# Revit family: PM-套管伸缩节
name_source: partatom
category: 管道附件
revit_build: Autodesk Revit 2016 (Build: 20150220_1215(x64)
units: mm (PartAtom-declared; Revit-internal decimal feet)

## family parameters
共享 = 否
加载时剪切的空心 = 否
圆形连接件大小 = 使用直径
基于工作平面 = 否
总是垂直 = 是
零件类型 = 阀门 - 插入

## types (22) — shared parameters
公司名称 = 品茗
制作 = pinming
材质 = <按类别>
版本号 = V1
类别 = 管道附件

## per-type parameters (varying)
| type | DN | L |
| PM-DN40 | 40 mm | 140 mm |
| PM-DN50 | 50 mm | 140 mm |
| PM-DN65 | 65 mm | 160 mm |
| PM-DN80 | 80 mm | 180 mm |
| PM-DN100 | 100 mm | 200 mm |
| PM-DN125 | 125 mm | 200 mm |
| PM-DN150 | 150 mm | 220 mm |
| PM-DN200 | 200 mm | 240 mm |
| PM-DN250 | 250 mm | 260 mm |
| PM-DN300 | 300 mm | 280 mm |
| PM-DN350 | 350 mm | 290 mm |
| PM-DN400 | 400 mm | 300 mm |
| PM-DN450 | 450 mm | 320 mm |
| PM-DN500 | 500 mm | 320 mm |
| PM-DN600 | 600 mm | 350 mm |
| PM-DN700 | 700 mm | 370 mm |
| PM-DN800 | 800 mm | 390 mm |
| PM-DN900 | 900 mm | 420 mm |
| PM-DN1000 | 1000 mm | 440 mm |
| PM-DN1200 | 1200 mm | 490 mm |
| PM-DN1400 | 1400 mm | 520 mm |
| PM-DN1600 | 1600 mm | 550 mm |
